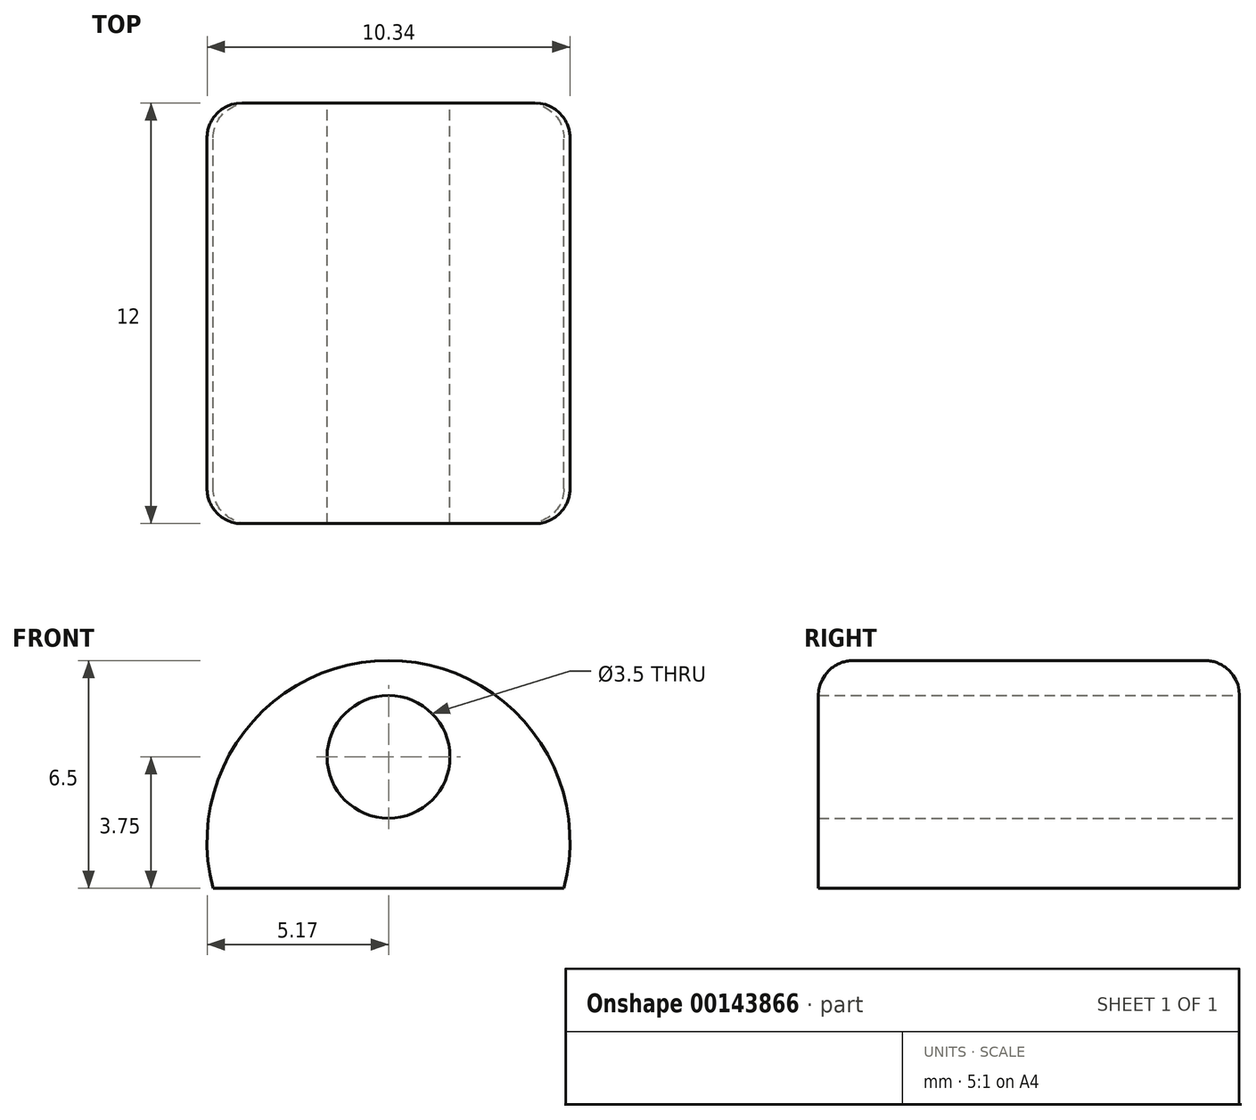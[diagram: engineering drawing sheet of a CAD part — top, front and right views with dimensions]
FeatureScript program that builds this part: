
annotation { "Feature Type Name" : "Feature", "Feature Type Description" : "" }
export const myFeature = defineFeature(function(context is Context, id is Id, definition is map)
    precondition{}
    {
        {
            var Q0;
            Q0=qCreatedBy(makeId("Front.planeOp"),FACE);
            var sketch = newSketch(context, id + "F0", { "sketchPlane" : qUnion([Q0])});
            skCircle(sketch, "E0", {"center": v(0, 0) * mm, "radius": 1.75 * mm});
            skLineSegment(sketch, "E1", {"start": v(-5, -3.75) * mm, "end": v(5, -3.75) * mm});
            skArc(sketch, "E2", {"start": v(5, -3.75) * mm, "mid": v(0, 2.75) * mm, "end": v(-5, -3.75) * mm});
            skSolve(sketch);
        }
        {
            var Q0;
            Q0=makeQuery(id+"F0.imprint","IMPRINT",FACE,{"disambiguationData":[TD([[makeQuery(id+"F0.imprint","IMPRINT",EDGE,{"derivedFrom":sQuery(id+"F0.wireOp",EDGE,"E0")}),-1.0]])]});
            extrude(context, id + "F1", {"entities" : qUnion([Q0]), "depth" : 12 * mm, "offsetDistance" : 25 * mm});
        }
        {
            var Q0;
            Q0=makeQuery(id+"F1.opExtrude","CAP_EDGE",EDGE,{"disambiguationData":[OSD([sQuery(id+"F0.wireOp",EDGE,"E2")])],"isStart":false});
            var Q1;
            Q1=makeQuery(id+"F1.opExtrude","CAP_EDGE",EDGE,{"disambiguationData":[OSD([sQuery(id+"F0.wireOp",EDGE,"E2")])],"isStart":true});
            fillet(context, id + "F2", {"entities" : qUnion([Q0, Q1]), "radius" : 1 * mm, "tangentPropagation" : true, "allowEdgeOverflow" : false});
        }
    });
